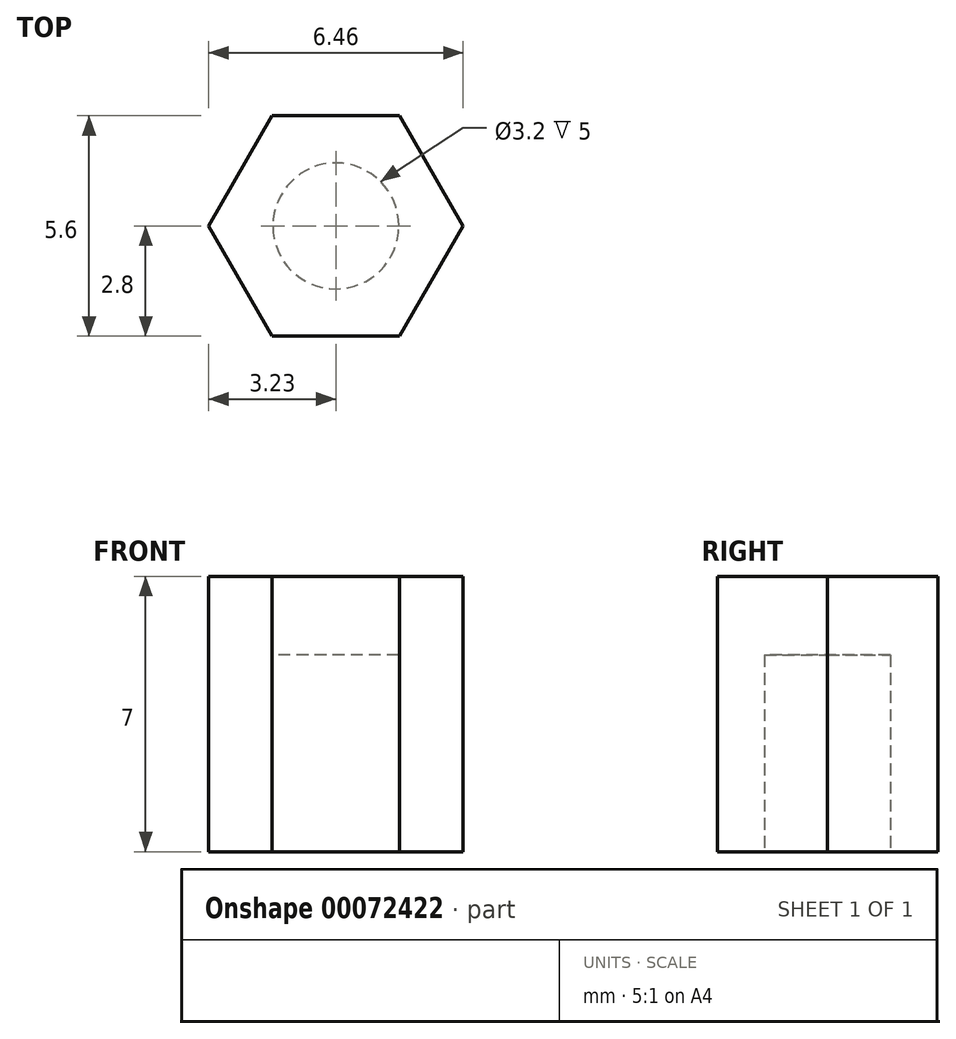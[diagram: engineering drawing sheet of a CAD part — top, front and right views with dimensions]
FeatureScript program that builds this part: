
annotation { "Feature Type Name" : "Feature", "Feature Type Description" : "" }
export const myFeature = defineFeature(function(context is Context, id is Id, definition is map)
    precondition{}
    {
        {
            assignVariable(context, id + "F0", {"name" : "h1", "anyValue" : 5});
        }
        {
            assignVariable(context, id + "F1", {"name" : "h2", "anyValue" : 2});
        }
        {
            var Q0;
            Q0=qCreatedBy(makeId("Top.planeOp"),FACE);
            var sketch = newSketch(context, id + "F2", { "sketchPlane" : qUnion([Q0])});
            skCircle(sketch, "E0", {"center": v(0, 0) * mm, "radius": 1.6 * mm});
            skCircle(sketch, "E1.cCircle", {"center": v(0, 0) * mm, "radius": 2.8 * mm, "construction": true});
            skLineSegment(sketch, "E1.0", {"start": v(1.62, -2.8) * mm, "end": v(-1.62, -2.8) * mm});
            skLineSegment(sketch, "E1.1", {"start": v(-1.62, -2.8) * mm, "end": v(-3.23, 0) * mm});
            skLineSegment(sketch, "E1.2", {"start": v(-3.23, 0) * mm, "end": v(-1.62, 2.8) * mm});
            skLineSegment(sketch, "E1.3", {"start": v(-1.62, 2.8) * mm, "end": v(1.62, 2.8) * mm});
            skLineSegment(sketch, "E1.4", {"start": v(1.62, 2.8) * mm, "end": v(3.23, 0) * mm});
            skLineSegment(sketch, "E1.5", {"start": v(3.23, 0) * mm, "end": v(1.62, -2.8) * mm});
            skPoint(sketch, "E1.0.midPoint", {"position": v(0, -2.8) * mm});
            skSolve(sketch);
        }
        {
            var Q0;
            Q0=makeQuery(id+"F2.imprint","IMPRINT",FACE,{"disambiguationData":[TD([[makeQuery(id+"F2.imprint","IMPRINT",EDGE,{"derivedFrom":sQuery(id+"F2.wireOp",EDGE,"E0")}),-1.0]])]});
            extrude(context, id + "F3", {"entities" : qUnion([Q0]), "depth" : (getVariable(context, 'h1')) * mm});
        }
        {
            var Q0;
            Q0=makeQuery(id+"F3.opExtrude","CAP_FACE",FACE,{"disambiguationData":[OSD([sQuery(id+"F2.wireOp",EDGE,"E0"),sQuery(id+"F2.wireOp",EDGE,"E1.0"),sQuery(id+"F2.wireOp",EDGE,"E1.1"),sQuery(id+"F2.wireOp",EDGE,"E1.2"),sQuery(id+"F2.wireOp",EDGE,"E1.3"),sQuery(id+"F2.wireOp",EDGE,"E1.4"),sQuery(id+"F2.wireOp",EDGE,"E1.5")])],"isStart":false});
            var sketch = newSketch(context, id + "F4", { "sketchPlane" : qUnion([Q0])});
            skCircle(sketch, "E2.cCircle", {"center": v(0, 0) * mm, "radius": 2.8 * mm, "construction": true});
            skLineSegment(sketch, "E2.0", {"start": v(1.62, -2.8) * mm, "end": v(-1.62, -2.8) * mm});
            skLineSegment(sketch, "E2.1", {"start": v(-1.62, -2.8) * mm, "end": v(-3.23, 0) * mm});
            skLineSegment(sketch, "E2.2", {"start": v(-3.23, 0) * mm, "end": v(-1.62, 2.8) * mm});
            skLineSegment(sketch, "E2.3", {"start": v(-1.62, 2.8) * mm, "end": v(1.62, 2.8) * mm});
            skLineSegment(sketch, "E2.4", {"start": v(1.62, 2.8) * mm, "end": v(3.23, 0) * mm});
            skLineSegment(sketch, "E2.5", {"start": v(3.23, 0) * mm, "end": v(1.62, -2.8) * mm});
            skPoint(sketch, "E2.0.midPoint", {"position": v(0, -2.8) * mm});
            skSolve(sketch);
        }
        {
            var Q0;
            Q0=makeQuery(id+"F4.imprint","IMPRINT",FACE,{"disambiguationData":[TD([[makeQuery(id+"F4.imprint","IMPRINT",EDGE,{"derivedFrom":makeQuery(id+"F3.opExtrude","CAP_EDGE",EDGE,{"disambiguationData":[OSD([sQuery(id+"F2.wireOp",EDGE,"E0")])],"isStart":false})}),1.0]])]});
            var Q1;
            Q1=makeQuery(id+"F4.imprint","IMPRINT",FACE,{"disambiguationData":[TD([[makeQuery(id+"F4.imprint","IMPRINT",EDGE,{"derivedFrom":sQuery(id+"F4.wireOp",EDGE,"E2.0")}),-1.0]])]});
            extrude(context, id + "F5", {"entities" : qUnion([Q0, Q1]), "operationType" : NewBodyOperationType.ADD, "depth" : (getVariable(context, 'h2')) * mm});
        }
    });
